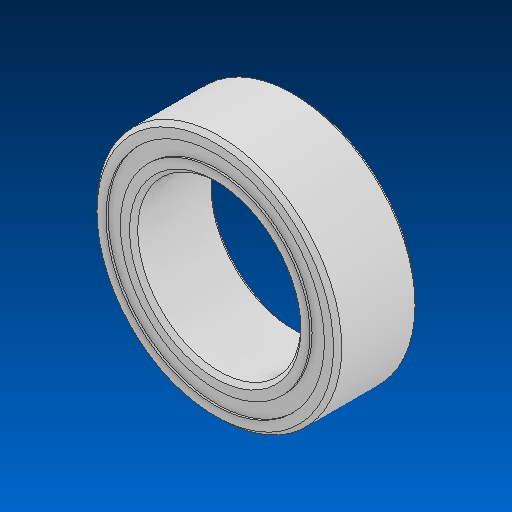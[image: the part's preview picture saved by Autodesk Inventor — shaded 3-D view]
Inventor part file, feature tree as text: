
AUTODESK INVENTOR PART (.ipt)
format: ipt  version: 2022.2 (Build 262287000, 287)  size: 608,256 bytes
history: native  units: in
note: dims shown in document units (in); Inventor stores cm internally (conversion verified against a paired STEP export)
features: other x11, revolve x5
ambient origin geometry x8: Origin, YZ Plane, XZ Plane, XY Plane, X Axis, Y Axis, Z Axis, Center Point
bodies: Solid1 (feature_tree), Solid2 (feature_tree), Solid3 (feature_tree), Solid4 (feature_tree), Solid5 (feature_tree), Solid6 (feature_tree), Solid7 (feature_tree), Solid8 (feature_tree), Solid9 (feature_tree), Solid10 (feature_tree), Solid11 (feature_tree), Solid12 (feature_tree), Solid13 (feature_tree), Solid14 (feature_tree), Solid15 (feature_tree), Solid16 (feature_tree)
feature tree (16):
  revolve  "Revolve1"  [1 undecoded]
  revolve  "Revolve3"  [1 undecoded]
  revolve  "Revolve4"  [1 undecoded]
  other  "CirPattern1[1]"
  other  "CirPattern1[2]"
  other  "CirPattern1[3]"
  other  "CirPattern1[4]"
  other  "CirPattern1[5]"
  other  "CirPattern1[6]"
  other  "CirPattern1[7]"
  other  "CirPattern1[8]"
  other  "CirPattern1[9]"
  other  "CirPattern1[10]"
  other  "CirPattern1[11]"
  revolve  "Revolve5[1]"  [1 undecoded]
  revolve  "Revolve5[2]"  [1 undecoded]
note: 5 required parameter values undecoded (feature->parameter linkage not recoverable at this tier; creation-order binding heuristic only, values carry confidence <= 0.55)
